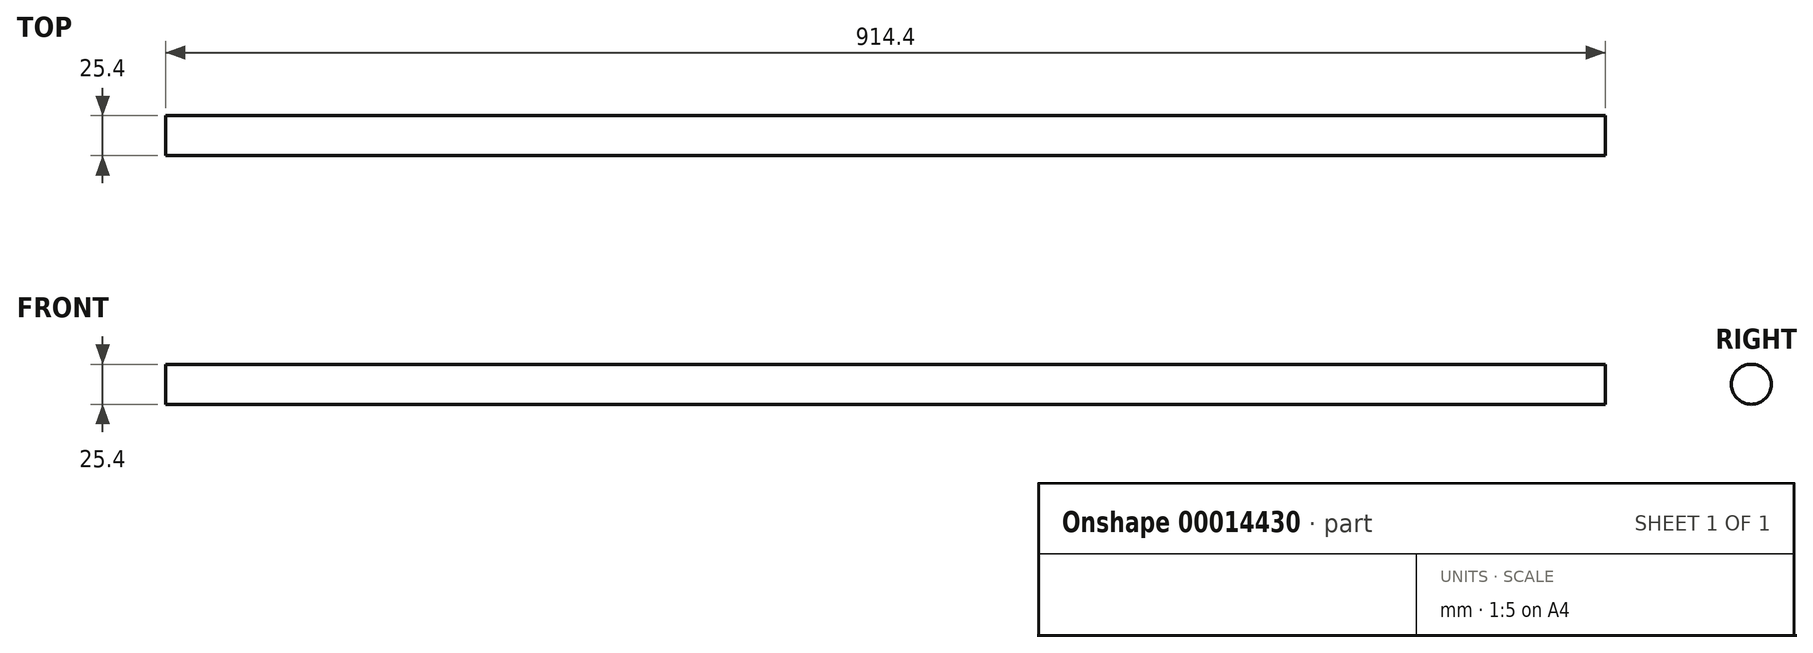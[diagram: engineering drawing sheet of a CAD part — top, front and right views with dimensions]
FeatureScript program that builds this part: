
annotation { "Feature Type Name" : "Feature", "Feature Type Description" : "" }
export const myFeature = defineFeature(function(context is Context, id is Id, definition is map)
    precondition{}
    {
        {
            var Q0;
            Q0=qCreatedBy(makeId("Right.planeOp"),FACE);
            var sketch = newSketch(context, id + "F0", { "sketchPlane" : qUnion([Q0])});
            skCircle(sketch, "E0", {"center": v(0, 0) * mm, "radius": 12.7 * mm});
            skSolve(sketch);
        }
        {
            var Q0;
            Q0=makeQuery(id+"F0.imprint","IMPRINT",FACE,{"disambiguationData":[TD([[makeQuery(id+"F0.imprint","IMPRINT",EDGE,{"derivedFrom":sQuery(id+"F0.wireOp",EDGE,"E0")}),1.0]])]});
            extrude(context, id + "F1", {"entities" : qUnion([Q0]), "endBound" : BoundingType.SYMMETRIC, "depth" : 914.4 * mm});
        }
    });
